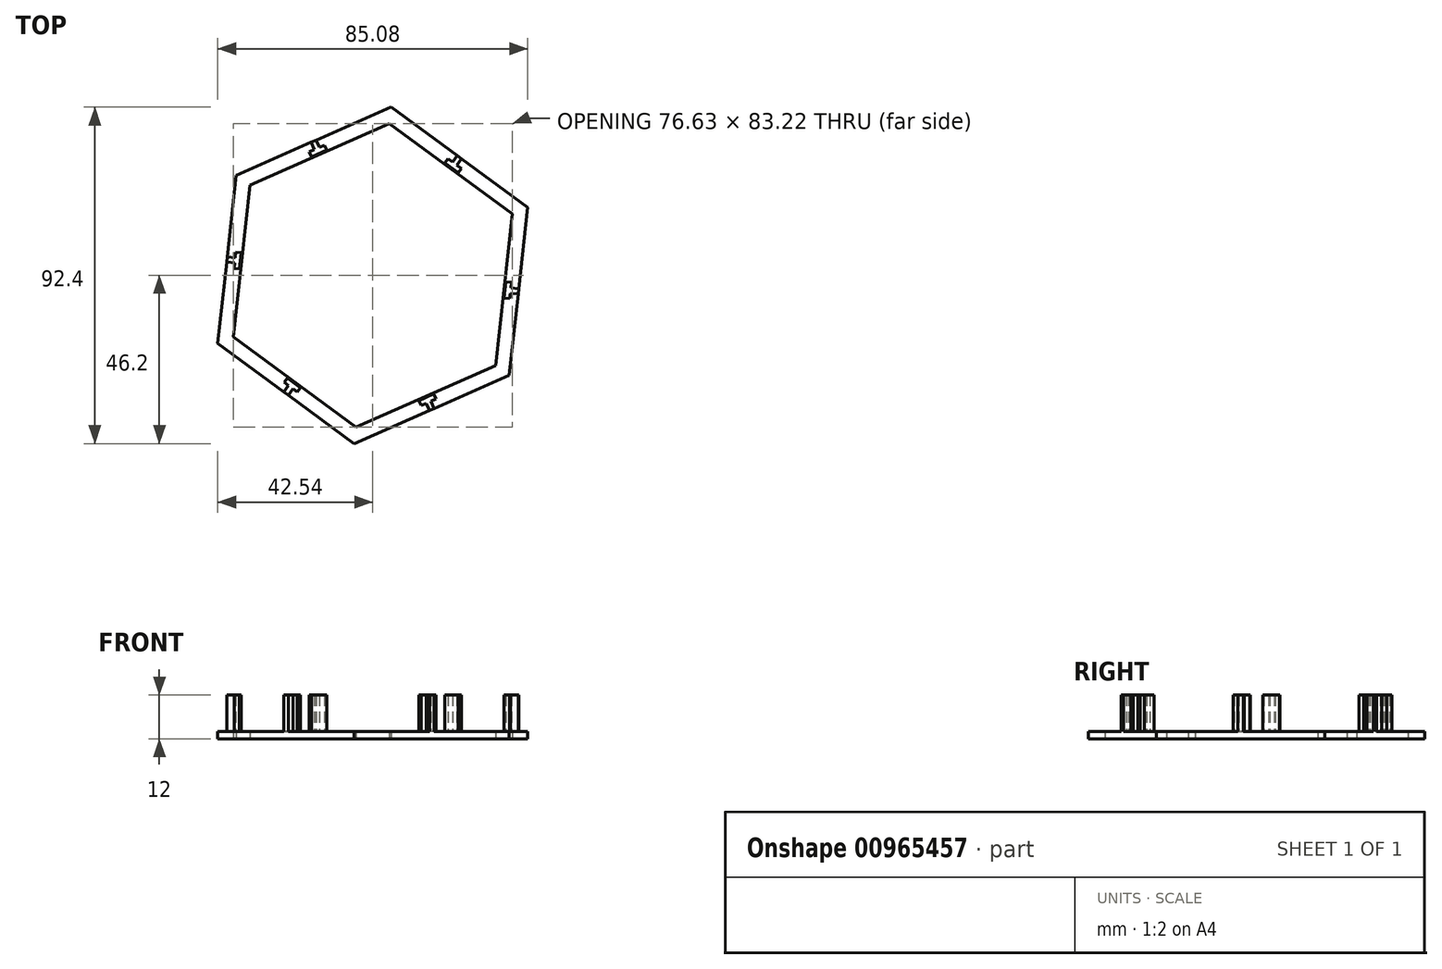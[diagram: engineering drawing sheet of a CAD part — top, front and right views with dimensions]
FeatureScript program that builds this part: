
annotation { "Feature Type Name" : "Feature", "Feature Type Description" : "" }
export const myFeature = defineFeature(function(context is Context, id is Id, definition is map)
    precondition{}
    {
        {
            var Q0;
            Q0=qCreatedBy(makeId("Top.planeOp"),FACE);
            var sketch = newSketch(context, id + "F0", { "sketchPlane" : qUnion([Q0])});
            skCircle(sketch, "E0.cCircle", {"center": v(0, 0) * mm, "radius": 40.25 * mm, "construction": true});
            skLineSegment(sketch, "E0.0", {"start": v(37.48, -27.48) * mm, "end": v(-5.06, -46.2) * mm});
            skLineSegment(sketch, "E0.1", {"start": v(-5.06, -46.2) * mm, "end": v(-42.54, -18.72) * mm});
            skLineSegment(sketch, "E0.2", {"start": v(-42.54, -18.72) * mm, "end": v(-37.48, 27.48) * mm});
            skLineSegment(sketch, "E0.3", {"start": v(-37.48, 27.48) * mm, "end": v(5.06, 46.2) * mm});
            skLineSegment(sketch, "E0.4", {"start": v(5.06, 46.2) * mm, "end": v(42.54, 18.72) * mm});
            skLineSegment(sketch, "E0.5", {"start": v(42.54, 18.72) * mm, "end": v(37.48, -27.48) * mm});
            skPoint(sketch, "E0.0.midPoint", {"position": v(16.2, -36.84) * mm});
            skLineSegment(sketch, "E1", {"start": v(0, 0) * mm, "end": v(-16.2, 36.84) * mm, "construction": true});
            skLineSegment(sketch, "E2", {"start": v(0, 0) * mm, "end": v(23.8, 32.46) * mm, "construction": true});
            skLineSegment(sketch, "E3", {"start": v(0, 0) * mm, "end": v(40.01, -4.38) * mm, "construction": true});
            skLineSegment(sketch, "E4", {"start": v(0, 0) * mm, "end": v(16.2, -36.84) * mm, "construction": true});
            skLineSegment(sketch, "E5", {"start": v(0, 0) * mm, "end": v(-23.8, -32.46) * mm, "construction": true});
            skLineSegment(sketch, "E6", {"start": v(0, 0) * mm, "end": v(-40.01, 4.38) * mm, "construction": true});
            skPoint(sketch, "E7", {"position": v(-36.33, 3.98) * mm});
            skCircle(sketch, "E8.cCircle", {"center": v(0, 0) * mm, "radius": 36.25 * mm, "construction": true});
            skLineSegment(sketch, "E8.0", {"start": v(-33.75, 24.75) * mm, "end": v(4.56, 41.6) * mm});
            skLineSegment(sketch, "E8.1", {"start": v(4.56, 41.6) * mm, "end": v(38.31, 16.86) * mm});
            skLineSegment(sketch, "E8.2", {"start": v(38.31, 16.86) * mm, "end": v(33.75, -24.75) * mm});
            skLineSegment(sketch, "E8.3", {"start": v(33.75, -24.75) * mm, "end": v(-4.56, -41.6) * mm});
            skLineSegment(sketch, "E8.4", {"start": v(-4.56, -41.6) * mm, "end": v(-38.31, -16.86) * mm});
            skLineSegment(sketch, "E8.5", {"start": v(-38.31, -16.86) * mm, "end": v(-33.75, 24.75) * mm});
            skPoint(sketch, "E8.0.midPoint", {"position": v(-14.6, 33.18) * mm});
            skSolve(sketch);
        }
        {
            var Q0;
            Q0=makeQuery(id+"F0.imprint","IMPRINT",FACE,{"disambiguationData":[TD([[makeQuery(id+"F0.imprint","IMPRINT",EDGE,{"derivedFrom":sQuery(id+"F0.wireOp",EDGE,"E0.0")}),-1.0]])]});
            var Q1;
            {var subQ0=sQuery(id+"F0.wireOp",EDGE,"PvMmcV7l-Ppxa-RKS9-J56H-K5XRcZqL9YKr");Q1=makeQuery(id+"F0.imprint","IMPRINT",FACE,{"disambiguationData":[TD([[makeQuery(id+"F0.imprint","IMPRINT",EDGE,{"derivedFrom":subQ0}),-1.0]])]});}
            extrude(context, id + "F1", {"entities" : qUnion([Q0, Q1]), "depth" : 2 * mm, "offsetDistance" : 25 * mm});
        }
        {
            var Q0;
            Q0=makeQuery(id+"F1.opExtrude","CAP_FACE",FACE,{"disambiguationData":[OSD([sQuery(id+"F0.wireOp",EDGE,"E0.0"),sQuery(id+"F0.wireOp",EDGE,"E0.1"),sQuery(id+"F0.wireOp",EDGE,"E0.2"),sQuery(id+"F0.wireOp",EDGE,"E0.3"),sQuery(id+"F0.wireOp",EDGE,"E0.4"),sQuery(id+"F0.wireOp",EDGE,"E0.5"),sQuery(id+"F0.wireOp",EDGE,"E8.0"),sQuery(id+"F0.wireOp",EDGE,"E8.1"),sQuery(id+"F0.wireOp",EDGE,"E8.2"),sQuery(id+"F0.wireOp",EDGE,"E8.3"),sQuery(id+"F0.wireOp",EDGE,"E8.4"),sQuery(id+"F0.wireOp",EDGE,"E8.5")])],"isStart":false});
            var sketch = newSketch(context, id + "F2", { "sketchPlane" : qUnion([Q0])});
            skLineSegment(sketch, "E9.0", {"start": v(-42.54, -18.72) * mm, "end": v(-37.48, 27.48) * mm});
            skLineSegment(sketch, "E9.1", {"start": v(-37.48, 27.48) * mm, "end": v(5.06, 46.2) * mm});
            skLineSegment(sketch, "E9.2", {"start": v(5.06, 46.2) * mm, "end": v(42.54, 18.72) * mm});
            skLineSegment(sketch, "E9.3", {"start": v(42.54, 18.72) * mm, "end": v(37.48, -27.48) * mm});
            skLineSegment(sketch, "E9.4", {"start": v(37.48, -27.48) * mm, "end": v(-5.06, -46.2) * mm});
            skLineSegment(sketch, "E9.5", {"start": v(-5.06, -46.2) * mm, "end": v(-42.54, -18.72) * mm});
            skPoint(sketch, "E10", {"position": v(-40.01, 4.38) * mm});
            skPoint(sketch, "E11", {"position": v(-16.2, 36.84) * mm});
            skPoint(sketch, "E12", {"position": v(23.8, 32.46) * mm});
            skPoint(sketch, "E13", {"position": v(40.01, -4.38) * mm});
            skPoint(sketch, "E14", {"position": v(16.2, -36.84) * mm});
            skPoint(sketch, "E15", {"position": v(-23.8, -32.46) * mm});
            skLineSegment(sketch, "E16", {"start": v(-39.93, 5.13) * mm, "end": v(-37.74, 4.9) * mm});
            skLineSegment(sketch, "E17", {"start": v(-37.74, 4.9) * mm, "end": v(-37.58, 6.38) * mm});
            skLineSegment(sketch, "E18", {"start": v(-37.58, 6.38) * mm, "end": v(-36.09, 6.22) * mm});
            skLineSegment(sketch, "E19", {"start": v(-36.09, 6.22) * mm, "end": v(-36.58, 1.74) * mm});
            skLineSegment(sketch, "E20", {"start": v(-36.58, 1.74) * mm, "end": v(-38.07, 1.9) * mm});
            skLineSegment(sketch, "E21", {"start": v(-38.07, 1.9) * mm, "end": v(-37.9, 3.4) * mm});
            skLineSegment(sketch, "E22", {"start": v(-37.9, 3.4) * mm, "end": v(-40.1, 3.64) * mm});
            skLineSegment(sketch, "E23", {"start": v(-24.4, -32.01) * mm, "end": v(-23.1, -30.24) * mm});
            skLineSegment(sketch, "E24", {"start": v(-23.1, -30.24) * mm, "end": v(-24.32, -29.35) * mm});
            skLineSegment(sketch, "E25", {"start": v(-24.32, -29.35) * mm, "end": v(-23.43, -28.14) * mm});
            skLineSegment(sketch, "E26", {"start": v(-23.43, -28.14) * mm, "end": v(-19.8, -30.8) * mm});
            skLineSegment(sketch, "E27", {"start": v(-19.8, -30.8) * mm, "end": v(-20.69, -32.01) * mm});
            skLineSegment(sketch, "E28", {"start": v(-20.69, -32.01) * mm, "end": v(-21.9, -31.13) * mm});
            skLineSegment(sketch, "E29", {"start": v(-21.9, -31.13) * mm, "end": v(-23.2, -32.9) * mm});
            skLineSegment(sketch, "E30", {"start": v(15.52, -37.14) * mm, "end": v(14.64, -35.13) * mm});
            skLineSegment(sketch, "E31", {"start": v(14.64, -35.13) * mm, "end": v(13.26, -35.73) * mm});
            skLineSegment(sketch, "E32", {"start": v(13.26, -35.73) * mm, "end": v(12.66, -34.36) * mm});
            skLineSegment(sketch, "E33", {"start": v(12.66, -34.36) * mm, "end": v(16.78, -32.55) * mm});
            skLineSegment(sketch, "E34", {"start": v(16.78, -32.55) * mm, "end": v(17.38, -33.92) * mm});
            skLineSegment(sketch, "E35", {"start": v(17.38, -33.92) * mm, "end": v(16, -34.53) * mm});
            skLineSegment(sketch, "E36", {"start": v(16, -34.53) * mm, "end": v(16.9, -36.54) * mm});
            skLineSegment(sketch, "E37", {"start": v(39.93, -5.13) * mm, "end": v(37.74, -4.9) * mm});
            skLineSegment(sketch, "E38", {"start": v(37.74, -4.9) * mm, "end": v(37.58, -6.38) * mm});
            skLineSegment(sketch, "E39", {"start": v(37.58, -6.38) * mm, "end": v(36.09, -6.22) * mm});
            skLineSegment(sketch, "E40", {"start": v(36.09, -6.22) * mm, "end": v(36.58, -1.74) * mm});
            skLineSegment(sketch, "E41", {"start": v(36.58, -1.74) * mm, "end": v(38.07, -1.9) * mm});
            skLineSegment(sketch, "E42", {"start": v(38.07, -1.9) * mm, "end": v(37.9, -3.4) * mm});
            skLineSegment(sketch, "E43", {"start": v(37.9, -3.4) * mm, "end": v(40.1, -3.64) * mm});
            skLineSegment(sketch, "E44", {"start": v(24.4, 32.01) * mm, "end": v(23.1, 30.24) * mm});
            skLineSegment(sketch, "E45", {"start": v(23.1, 30.24) * mm, "end": v(24.32, 29.35) * mm});
            skLineSegment(sketch, "E46", {"start": v(24.32, 29.35) * mm, "end": v(23.43, 28.14) * mm});
            skLineSegment(sketch, "E47", {"start": v(23.43, 28.14) * mm, "end": v(19.8, 30.8) * mm});
            skLineSegment(sketch, "E48", {"start": v(19.8, 30.8) * mm, "end": v(20.69, 32.01) * mm});
            skLineSegment(sketch, "E49", {"start": v(20.69, 32.01) * mm, "end": v(21.9, 31.13) * mm});
            skLineSegment(sketch, "E50", {"start": v(21.9, 31.13) * mm, "end": v(23.2, 32.9) * mm});
            skLineSegment(sketch, "E51", {"start": v(-15.52, 37.14) * mm, "end": v(-14.64, 35.13) * mm});
            skLineSegment(sketch, "E52", {"start": v(-14.64, 35.13) * mm, "end": v(-13.26, 35.73) * mm});
            skLineSegment(sketch, "E53", {"start": v(-13.26, 35.73) * mm, "end": v(-12.66, 34.36) * mm});
            skLineSegment(sketch, "E54", {"start": v(-12.66, 34.36) * mm, "end": v(-16.78, 32.55) * mm});
            skLineSegment(sketch, "E55", {"start": v(-16.78, 32.55) * mm, "end": v(-17.38, 33.92) * mm});
            skLineSegment(sketch, "E56", {"start": v(-17.38, 33.92) * mm, "end": v(-16, 34.53) * mm});
            skLineSegment(sketch, "E57", {"start": v(-16, 34.53) * mm, "end": v(-16.9, 36.54) * mm});
            skSolve(sketch);
        }
        {
            var Q0;
            {var subQ0=sQuery(id+"F2.wireOp",EDGE,"E51");Q0=makeQuery(id+"F2.imprint","IMPRINT",FACE,{"disambiguationData":[TD([[makeQuery(id+"F2.imprint","IMPRINT",EDGE,{"derivedFrom":subQ0}),-1.0]])]});}
            var Q1;
            {var subQ0=sQuery(id+"F2.wireOp",EDGE,"E44");Q1=makeQuery(id+"F2.imprint","IMPRINT",FACE,{"disambiguationData":[TD([[makeQuery(id+"F2.imprint","IMPRINT",EDGE,{"derivedFrom":subQ0}),-1.0]])]});}
            var Q2;
            {var subQ0=sQuery(id+"F2.wireOp",EDGE,"E37");Q2=makeQuery(id+"F2.imprint","IMPRINT",FACE,{"disambiguationData":[TD([[makeQuery(id+"F2.imprint","IMPRINT",EDGE,{"derivedFrom":subQ0}),-1.0]])]});}
            var Q3;
            {var subQ0=sQuery(id+"F2.wireOp",EDGE,"E30");Q3=makeQuery(id+"F2.imprint","IMPRINT",FACE,{"disambiguationData":[TD([[makeQuery(id+"F2.imprint","IMPRINT",EDGE,{"derivedFrom":subQ0}),-1.0]])]});}
            var Q4;
            {var subQ0=sQuery(id+"F2.wireOp",EDGE,"E23");Q4=makeQuery(id+"F2.imprint","IMPRINT",FACE,{"disambiguationData":[TD([[makeQuery(id+"F2.imprint","IMPRINT",EDGE,{"derivedFrom":subQ0}),-1.0]])]});}
            var Q5;
            {var subQ0=sQuery(id+"F2.wireOp",EDGE,"E16");Q5=makeQuery(id+"F2.imprint","IMPRINT",FACE,{"disambiguationData":[TD([[makeQuery(id+"F2.imprint","IMPRINT",EDGE,{"derivedFrom":subQ0}),-1.0]])]});}
            extrude(context, id + "F3", {"entities" : qUnion([Q0, Q1, Q2, Q3, Q4, Q5]), "operationType" : NewBodyOperationType.ADD, "depth" : 10 * mm, "offsetDistance" : 25 * mm});
        }
    });
